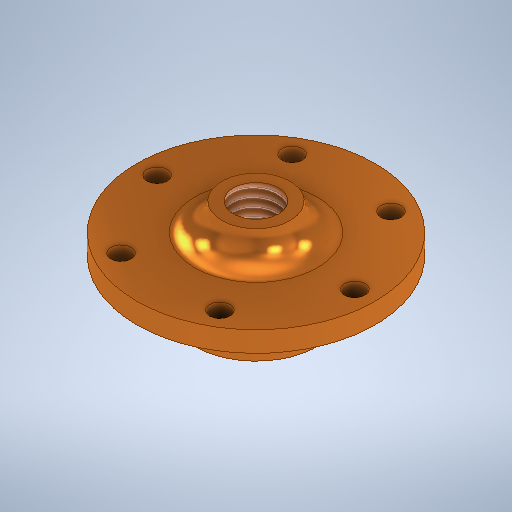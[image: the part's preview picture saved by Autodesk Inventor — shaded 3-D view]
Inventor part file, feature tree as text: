
AUTODESK INVENTOR PART (.ipt)
format: ipt  version: 2025.1 (Build 291241000, 241)  size: 324,096 bytes
history: native  units: mm
features: sketch x4, hole x3, plane x1, revolve x1, pattern_circular x1
ambient origin geometry x8: Origin, YZ Plane, XZ Plane, XY Plane, X Axis, Y Axis, Z Axis, Center Point
bodies: Body1 (feature_tree)
feature tree (10):
  plane  "Work Plane1"
  revolve  "Revolution2"  [1 undecoded]
  hole  "Hole1"  [1 undecoded]
  hole  "Hole2"  [1 undecoded]
  hole  "Hole3"  [1 undecoded]
  pattern_circular  "Circular Pattern1"  [2 undecoded]
  sketch  "Sketch3"  dims[d3=0.0mm d10=4.0mm]
  sketch  "Sketch4"  dims[d11=3.0mm d12=35.0mm]
  sketch  "Sketch5"  dims[d13=7.0mm d14=18.0mm]
  sketch  "Sketch6"  dims[d15=90.0deg d16=6.647mm d17=8.0mm d18=8.0mm d19=8.0mm d20=90.0deg d21=8.0mm d22=0.0mm d23=5.0mm d24=8.0mm d25=4.0mm d26=2.0mm d27=90.0deg d28=6.0mm d29=0.0mm d30=30.0deg d31=29.0mm d32=3.0mm d33=6.0mm d34=4.0mm d35=2.0mm d36=90.0deg d37=8.0mm d38=0.0mm d39=60.0mm d40=360.0deg]
note: 6 required parameter values undecoded (feature->parameter linkage not recoverable at this tier; creation-order binding heuristic only, values carry confidence <= 0.55)